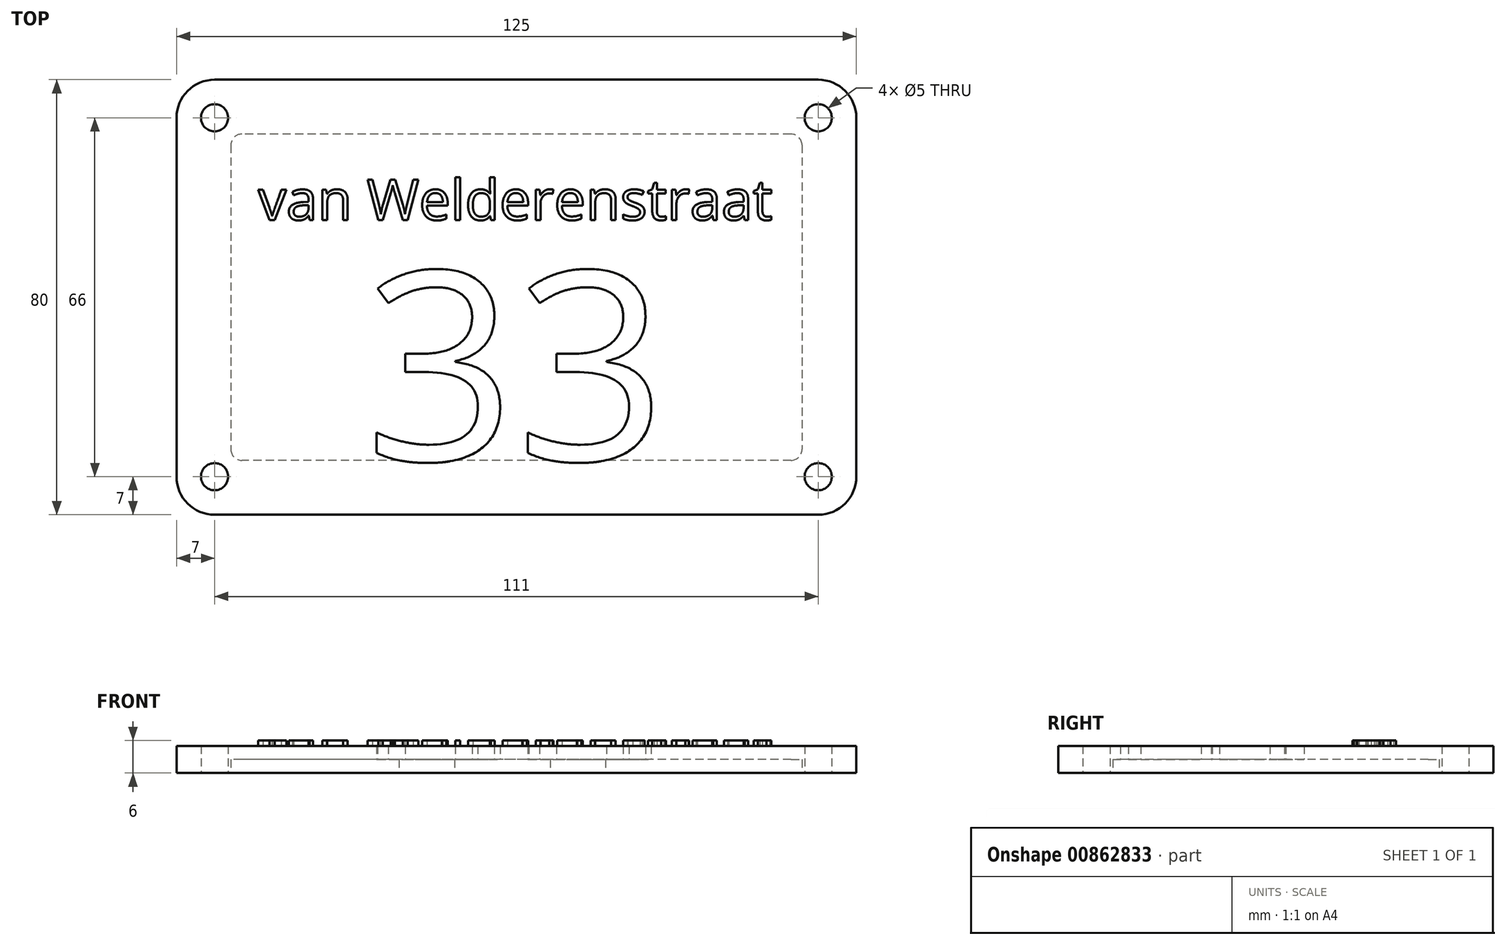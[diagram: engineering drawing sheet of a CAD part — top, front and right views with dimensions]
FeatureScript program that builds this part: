
annotation { "Feature Type Name" : "Feature", "Feature Type Description" : "" }
export const myFeature = defineFeature(function(context is Context, id is Id, definition is map)
    precondition{}
    {
        {
            var Q0;
            Q0=qCreatedBy(makeId("Top.planeOp"),FACE);
            var sketch = newSketch(context, id + "F0", { "sketchPlane" : qUnion([Q0])});
            skLineSegment(sketch, "E0.bottom", {"start": v(55.5, -40) * mm, "end": v(-55.5, -40) * mm});
            skLineSegment(sketch, "E0.top", {"start": v(55.5, 40) * mm, "end": v(-55.5, 40) * mm});
            skLineSegment(sketch, "E0.left", {"start": v(62.5, -33) * mm, "end": v(62.5, 33) * mm});
            skLineSegment(sketch, "E0.right", {"start": v(-62.5, -33) * mm, "end": v(-62.5, 33) * mm});
            skPoint(sketch, "E0.middle", {"position": v(0, 0) * mm});
            skPoint(sketch, "E1.visualSharp", {"position": v(-62.5, 40) * mm});
            skArc(sketch, "E1.filletArc", {"start": v(-55.5, 40) * mm, "mid": v(-60.45, 37.95) * mm, "end": v(-62.5, 33) * mm});
            skPoint(sketch, "E2.visualSharp", {"position": v(62.5, 40) * mm});
            skArc(sketch, "E2.filletArc", {"start": v(62.5, 33) * mm, "mid": v(60.45, 37.95) * mm, "end": v(55.5, 40) * mm});
            skPoint(sketch, "E3.visualSharp", {"position": v(62.5, -40) * mm});
            skArc(sketch, "E3.filletArc", {"start": v(55.5, -40) * mm, "mid": v(60.45, -37.95) * mm, "end": v(62.5, -33) * mm});
            skPoint(sketch, "E4.visualSharp", {"position": v(-62.5, -40) * mm});
            skArc(sketch, "E4.filletArc", {"start": v(-62.5, -33) * mm, "mid": v(-60.45, -37.95) * mm, "end": v(-55.5, -40) * mm});
            skCircle(sketch, "E5", {"center": v(-55.5, 33) * mm, "radius": 2.5 * mm});
            skCircle(sketch, "E6", {"center": v(55.5, 33) * mm, "radius": 2.5 * mm});
            skCircle(sketch, "E7", {"center": v(55.5, -33) * mm, "radius": 2.5 * mm});
            skCircle(sketch, "E8", {"center": v(-55.5, -33) * mm, "radius": 2.5 * mm});
            skSolve(sketch);
        }
        {
            var Q0;
            Q0 = qSketchRegion(id + "F0", true);
            extrude(context, id + "F1", {"entities" : qUnion([Q0]), "depth" : 5 * mm, "offsetDistance" : 25 * mm});
        }
        {
            var Q0;
            Q0=qCreatedBy(makeId("Top.planeOp"),FACE);
            var sketch = newSketch(context, id + "F2", { "sketchPlane" : qUnion([Q0])});
            skLineSegment(sketch, "E9.bottom", {"start": v(50.5, 30) * mm, "end": v(-50.5, 30) * mm});
            skLineSegment(sketch, "E9.top", {"start": v(50.5, -30) * mm, "end": v(-50.5, -30) * mm});
            skLineSegment(sketch, "E9.left", {"start": v(52.5, 28) * mm, "end": v(52.5, -28) * mm});
            skLineSegment(sketch, "E9.right", {"start": v(-52.5, 28) * mm, "end": v(-52.5, -28) * mm});
            skPoint(sketch, "E9.middle", {"position": v(0, 0) * mm});
            skPoint(sketch, "E10.visualSharp", {"position": v(-52.5, -30) * mm});
            skArc(sketch, "E10.filletArc", {"start": v(-52.5, -28) * mm, "mid": v(-51.91, -29.41) * mm, "end": v(-50.5, -30) * mm});
            skPoint(sketch, "E11.visualSharp", {"position": v(52.5, -30) * mm});
            skArc(sketch, "E11.filletArc", {"start": v(50.5, -30) * mm, "mid": v(51.91, -29.41) * mm, "end": v(52.5, -28) * mm});
            skPoint(sketch, "E12.visualSharp", {"position": v(52.5, 30) * mm});
            skArc(sketch, "E12.filletArc", {"start": v(52.5, 28) * mm, "mid": v(51.91, 29.41) * mm, "end": v(50.5, 30) * mm});
            skPoint(sketch, "E13.visualSharp", {"position": v(-52.5, 30) * mm});
            skArc(sketch, "E13.filletArc", {"start": v(-50.5, 30) * mm, "mid": v(-51.91, 29.41) * mm, "end": v(-52.5, 28) * mm});
            skSolve(sketch);
        }
        {
            var Q0;
            Q0=makeQuery(id+"F2.imprint","IMPRINT",FACE,{"disambiguationData":[TD([[makeQuery(id+"F2.imprint","IMPRINT",EDGE,{"derivedFrom":sQuery(id+"F2.wireOp",EDGE,"E9.bottom")}),1.0]])]});
            extrude(context, id + "F3", {"entities" : qUnion([Q0]), "operationType" : NewBodyOperationType.REMOVE, "depth" : 2.5 * mm, "offsetDistance" : 25 * mm});
        }
        {
            var Q0;
            Q0=makeQuery(id+"F1.opExtrude","CAP_FACE",FACE,{"disambiguationData":[OSD([sQuery(id+"F0.wireOp",EDGE,"E0.bottom"),sQuery(id+"F0.wireOp",EDGE,"E0.top"),sQuery(id+"F0.wireOp",EDGE,"E0.left"),sQuery(id+"F0.wireOp",EDGE,"E0.right"),sQuery(id+"F0.wireOp",EDGE,"E1.filletArc"),sQuery(id+"F0.wireOp",EDGE,"E2.filletArc"),sQuery(id+"F0.wireOp",EDGE,"E3.filletArc"),sQuery(id+"F0.wireOp",EDGE,"E4.filletArc"),sQuery(id+"F0.wireOp",EDGE,"E5"),sQuery(id+"F0.wireOp",EDGE,"E6"),sQuery(id+"F0.wireOp",EDGE,"E7"),sQuery(id+"F0.wireOp",EDGE,"E8")])],"isStart":false});
            var sketch = newSketch(context, id + "F4", { "sketchPlane" : qUnion([Q0])});
            skText(sketch, "E14", { "text": "van Welderenstraat", "fontName": "OpenSans-Regular.ttf"});
            const initialGuessF4  = {"E14": [-0.0475, 0.01421, 1, 0, 0.00746]};
            skSetInitialGuess(sketch, initialGuessF4);
            skSolve(sketch);
        }
        {
            var Q0;
            Q0 = qSketchRegion(id + "F4", true);
            extrude(context, id + "F5", {"entities" : qUnion([Q0]), "operationType" : NewBodyOperationType.ADD, "depth" : 1 * mm, "offsetDistance" : 25 * mm});
        }
        {
            var Q0;
            Q0=qCreatedBy(makeId("Top.planeOp"),FACE);
            var sketch = newSketch(context, id + "F6", { "sketchPlane" : qUnion([Q0])});
            skText(sketch, "E15", { "text": "33", "fontName": "OpenSans-Regular.ttf"});
            const initialGuessF6  = {"E15": [-0.02794, -0.03, 1, 0, 0.035]};
            skSetInitialGuess(sketch, initialGuessF6);
            skSolve(sketch);
        }
        {
            var Q0;
            Q0 = qSketchRegion(id + "F6", true);
            extrude(context, id + "F7", {"entities" : qUnion([Q0]), "operationType" : NewBodyOperationType.REMOVE, "endBound" : BoundingType.THROUGH_ALL, "depth" : 25 * mm, "offsetDistance" : 25 * mm});
        }
    });
